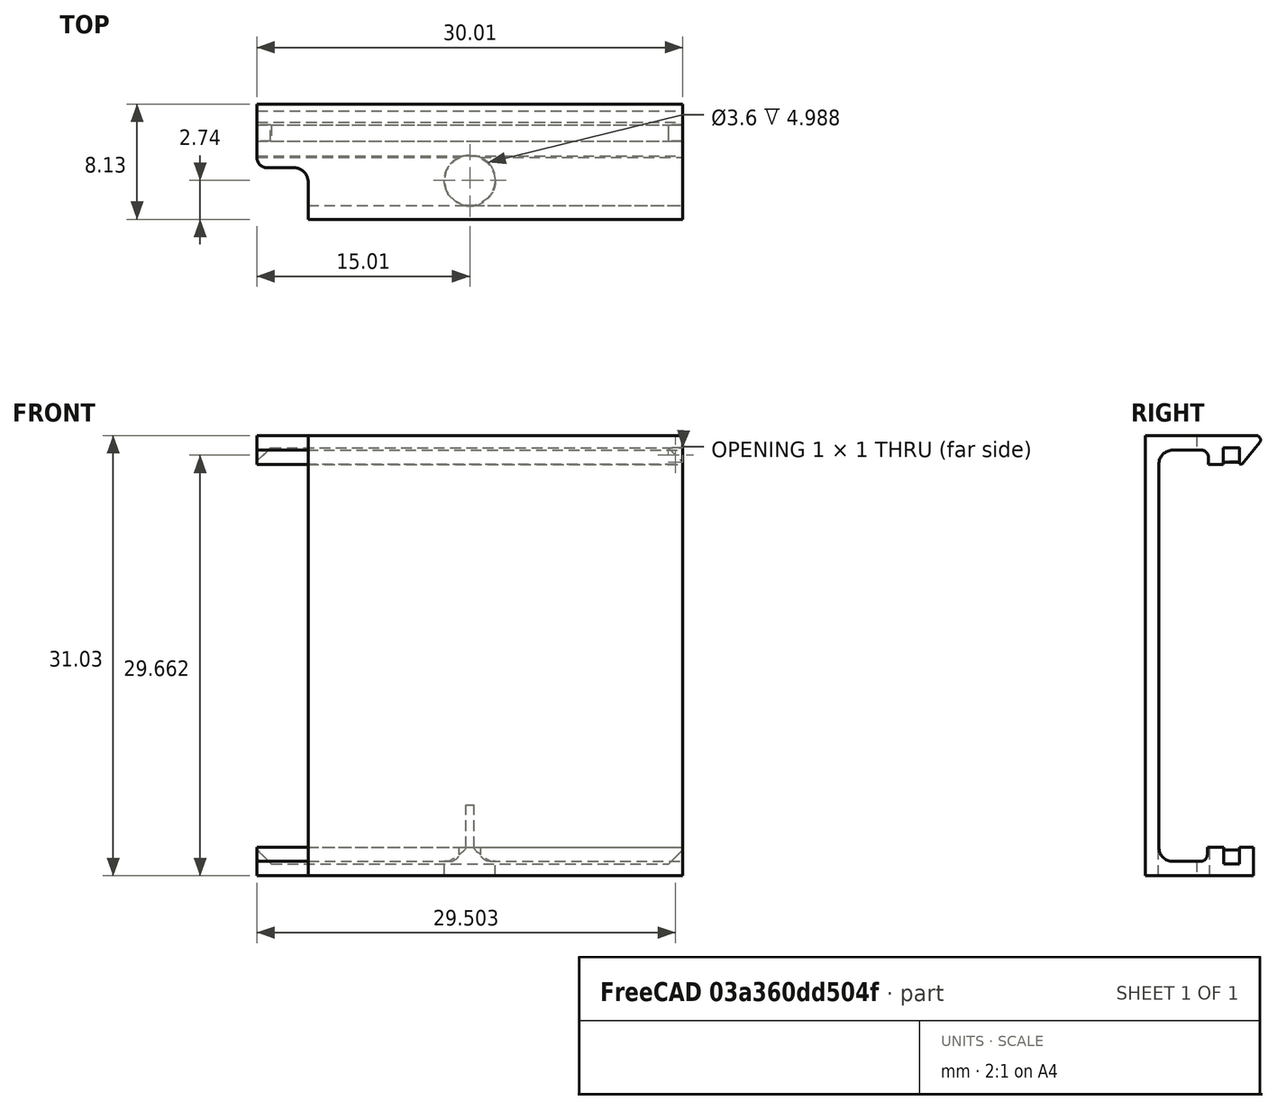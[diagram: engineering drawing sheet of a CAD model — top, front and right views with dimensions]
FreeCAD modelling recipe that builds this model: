
FCSTD DOCUMENT  (FreeCAD 0.18.4R)
Label: GPSAntennaClip
License: All rights reserved
LicenseURL: http://en.wikipedia.org/wiki/All_rights_reserved
objects: Part::Fillet×7, Sketcher::SketchObject×5, PartDesign::Pad×5, Part::Cut×2, Part::Box×1, Part::MultiFuse×1, Part::Cylinder×1, Mesh::Feature×1
note: 27 computed .brp shape members not serialized (recipe doc carries the construction recipe); baked Part::Feature solids carry a one-line shape summary decoded from their .brp

FEATURE [Sketcher::SketchObject] Sketch
  MapMode = 5
  Placement = pos=(-13.6,0,29.03) rot=(0,1,0;1.5708rad)
  sketch-geometry (21):
    g0: LineSegment StartX=-13.988 StartY=-10.6776 StartZ=0 EndX=15.0066 EndY=-10.6776 EndZ=0
    g1: LineSegment StartX=16.0148 StartY=-11.6432 StartZ=0 EndX=-15.0001 EndY=-11.6432 EndZ=0
    g2: LineSegment StartX=16.0192 StartY=-4.00811 StartZ=0 EndX=16.0148 EndY=-11.6432 EndZ=0
    g3: LineSegment StartX=14.0057 StartY=-4.0048 StartZ=0 EndX=14.0014 EndY=-4.99117 EndZ=0
    g4: LineSegment StartX=14.0057 StartY=-4.0048 StartZ=0 EndX=16.0192 EndY=-4.00811 EndZ=0
    g5: LineSegment StartX=14.0014 StartY=-4.99117 StartZ=0 EndX=15.182 EndY=-4.98967 EndZ=0
    g6: LineSegment StartX=15.182 StartY=-4.98967 StartZ=0 EndX=15.1785 EndY=-6.1172 EndZ=0
    g7: LineSegment StartX=15.1785 StartY=-6.1172 StartZ=0 EndX=14.0167 EndY=-6.11499 EndZ=0
    g8: LineSegment StartX=14.0167 StartY=-6.11499 StartZ=0 EndX=14.0167 EndY=-7.25961 EndZ=0
    g9: LineSegment StartX=-12.9698 StartY=-6.12023 StartZ=0 EndX=-14.1555 EndY=-6.12364 EndZ=0
    g10: LineSegment StartX=-14.1555 StartY=-6.12364 StartZ=0 EndX=-14.153 EndY=-4.98627 EndZ=0
    g11: LineSegment StartX=-14.153 StartY=-4.98627 StartZ=0 EndX=-13.0087 EndY=-4.9864 EndZ=0
    g12: LineSegment StartX=-13.0087 StartY=-4.9864 StartZ=0 EndX=-13.0047 EndY=-4.80508 EndZ=0
    g13: LineSegment StartX=-13.0047 StartY=-4.80508 StartZ=0 EndX=-15.0152 EndY=-3.17983 EndZ=0
    g14: LineSegment StartX=-15.0152 StartY=-3.17983 StartZ=0 EndX=-15.0001 EndY=-11.6432 EndZ=0
    g15: LineSegment StartX=14.0167 StartY=-7.25961 StartZ=0 EndX=15.0074 EndY=-7.25703 EndZ=0
    g16: LineSegment StartX=15.0074 StartY=-7.25703 StartZ=0 EndX=15.0066 EndY=-10.6776 EndZ=0
    g17: LineSegment StartX=-12.9698 StartY=-6.12023 StartZ=0 EndX=-12.9832 EndY=-7.18011 EndZ=0
    g18: LineSegment StartX=-12.9721 StartY=-9.37554 StartZ=0 EndX=-12.9816 EndY=-9.37554 EndZ=0
    g19: LineSegment StartX=-12.9832 StartY=-7.18011 StartZ=0 EndX=-13.9903 EndY=-7.18166 EndZ=0
    g20: LineSegment StartX=-13.9903 StartY=-7.18166 StartZ=0 EndX=-13.988 EndY=-10.6776 EndZ=0
  constraints (22):
    c: Horizontal(g0)
    c: Horizontal(g1)
    c: Coincident(g1,g2)
    c: Coincident(g4,g3)
    c: Coincident(g3,g5)
    c: Coincident(g5,g6)
    c: Coincident(g6,g7)
    c: Coincident(g8,g7)
    c: Coincident(g4,g2)
    c: Coincident(g9,g10)
    c: Coincident(g10,g11)
    c: Coincident(g11,g12)
    c: Coincident(g12,g13)
    c: Coincident(g14,g13)
    c: Coincident(g14,g1)
    c: Coincident(g15,g8)
    c: Coincident(g15,g16)
    c: Coincident(g16,g0)
    c: Coincident(g9,g17)
    c: Coincident(g17,g19)
    c: Coincident(g19,g20)
    c: Coincident(g0,g20)
FEATURE [PartDesign::Pad] Pad
  Length = 30
  Length2 = 100
  Placement = pos=(-13.6,0,29.03) rot=(0,1,0;1.5708rad)
  Profile = -> Sketch
  Type = 0
FEATURE [Sketcher::SketchObject] Sketch004
  MapMode = 5
  Placement = pos=(-6.6,-4.95,19.85) rot=(1,0,0;1.5708rad)
  sketch-geometry (3):
    g0: LineSegment StartX=-7.00166 StartY=-5.01077 StartZ=0 EndX=-6.98953 EndY=-6.02972 EndZ=0
    g1: LineSegment StartX=-6.98953 StartY=-6.02972 StartZ=0 EndX=-5.96627 EndY=-6.02972 EndZ=0
    g2: LineSegment StartX=-7.00166 StartY=-5.01077 StartZ=0 EndX=-5.96627 EndY=-6.02972 EndZ=0
  constraints (3):
    c: Coincident(g0,g1)
    c: Coincident(g2,g0)
    c: Coincident(g2,g1)
FEATURE [PartDesign::Pad] Pad004  label="stopper002"
  Length = 1.2
  Length2 = 100
  Placement = pos=(-6.6,-4.95,19.85) rot=(1,0,0;1.5708rad)
  Profile = -> Sketch004
  Type = 0
FEATURE [Sketcher::SketchObject] Sketch006
  MapMode = 5
  Placement = pos=(16.4,-4.95,13.85) rot=(1,0,0;1.5708rad)
  sketch-geometry (3):
    g0: LineSegment StartX=-0.005347 StartY=0.971544 StartZ=0 EndX=-0.005347 EndY=-0.027131 EndZ=0
    g1: LineSegment StartX=-0.005347 StartY=-0.027131 StartZ=0 EndX=-1.00402 EndY=-0.027124 EndZ=0
    g2: LineSegment StartX=-1.00402 StartY=-0.027124 StartZ=0 EndX=-0.005347 EndY=0.971544 EndZ=0
  constraints (3):
    c: Coincident(g0,g1)
    c: Coincident(g1,g2)
    c: Coincident(g2,g0)
FEATURE [PartDesign::Pad] Pad006  label="stopper003"
  Length = 1.2
  Length2 = 100
  Placement = pos=(16.4,-4.95,13.85) rot=(1,0,0;1.5708rad)
  Profile = -> Sketch006
  Type = 0
FEATURE [Sketcher::SketchObject] Sketch007
  MapMode = 5
  Placement = pos=(16.4,-4.95,42.2) rot=(1,0,0;1.5708rad)
  sketch-geometry (3):
    g0: LineSegment StartX=-0.005347 StartY=0.971544 StartZ=0 EndX=-0.005347 EndY=-0.027131 EndZ=0
    g1: LineSegment StartX=-0.005347 StartY=-0.027131 StartZ=0 EndX=-1.00779 EndY=0.969763 EndZ=0
    g2: LineSegment StartX=-1.00779 StartY=0.969763 StartZ=0 EndX=-0.005347 EndY=0.971544 EndZ=0
  constraints (3):
    c: Coincident(g0,g1)
    c: Coincident(g1,g2)
    c: Coincident(g2,g0)
FEATURE [PartDesign::Pad] Pad007  label="stopper004"
  Length = 1.2
  Length2 = 100
  Placement = pos=(16.4,-4.95,42.2) rot=(1,0,0;1.5708rad)
  Profile = -> Sketch007
  Type = 0
FEATURE [Sketcher::SketchObject] Sketch008
  MapMode = 5
  Placement = pos=(-12.6,-4.95,42.25) rot=(1,0,0;1.5708rad)
  sketch-geometry (3):
    g0: LineSegment StartX=-0.005347 StartY=0.971544 StartZ=0 EndX=-1.00207 EndY=-0.002707 EndZ=0
    g1: LineSegment StartX=-1.00207 StartY=-0.002707 StartZ=0 EndX=-1.00779 EndY=0.969763 EndZ=0
    g2: LineSegment StartX=-1.00779 StartY=0.969763 StartZ=0 EndX=-0.005347 EndY=0.971544 EndZ=0
  constraints (3):
    c: Coincident(g0,g1)
    c: Coincident(g1,g2)
    c: Coincident(g2,g0)
FEATURE [PartDesign::Pad] Pad008  label="stopper001"
  Length = 1.2
  Length2 = 100
  Placement = pos=(-12.6,-4.95,42.25) rot=(1,0,0;1.5708rad)
  Profile = -> Sketch008
  Type = 0
FEATURE [Part::Box] Box  label="Würfel"
  AttacherType = Attacher::AttachEngine3D
  Height = 33
  Length = 5
  Placement = pos=(-15,-13,12) rot=(0,0,1;0rad)
  Width = 5
FEATURE [Part::Fillet] Fillet
  Base = -> Box
  Edges = 1 edges r=1: [Edge7]
FEATURE [Part::MultiFuse] Fusion
  Shapes = -> [Pad,Pad008,Pad007,Pad006,Pad004]
FEATURE [Part::Cut] Cut
  Base = -> Fusion
  Tool = -> Fillet
FEATURE [Part::Fillet] Fillet001
  Base = -> Cut
  Edges = 1 edges r=0.7: [Edge110]
FEATURE [Part::Fillet] Fillet002
  Base = -> Fillet001
  Edges = 1 edges r=0.7: [Edge124]
FEATURE [Part::Fillet] Fillet003
  Base = -> Fillet002
  Edges = 1 edges r=0.3: [Edge55]
FEATURE [Part::Cylinder] Cylinder  label="Zylinder"
  Angle = 360
  AttacherType = Attacher::AttachEngine3D
  Height = 10
  Placement = pos=(1.4,-8.9,8) rot=(0,0,1;0rad)
  Radius = 1.8
FEATURE [Part::Cut] Cut001
  Base = -> Fillet003
  Tool = -> Cylinder
FEATURE [Part::Fillet] Fillet004
  Base = -> Cut001
  Edges = 3 edges r=1: [Edge33,Edge82,Edge86]
FEATURE [Part::Fillet] Fillet005
  Base = -> Fillet004
  Edges = 2 edges r=0.5: [Edge76,Edge123]
FEATURE [Part::Fillet] Fillet006
  Base = -> Fillet005
  Edges = 1 edges r=0.5: [Edge53]
FEATURE [Mesh::Feature] Mesh  label="Fillet006 (Meshed)"
